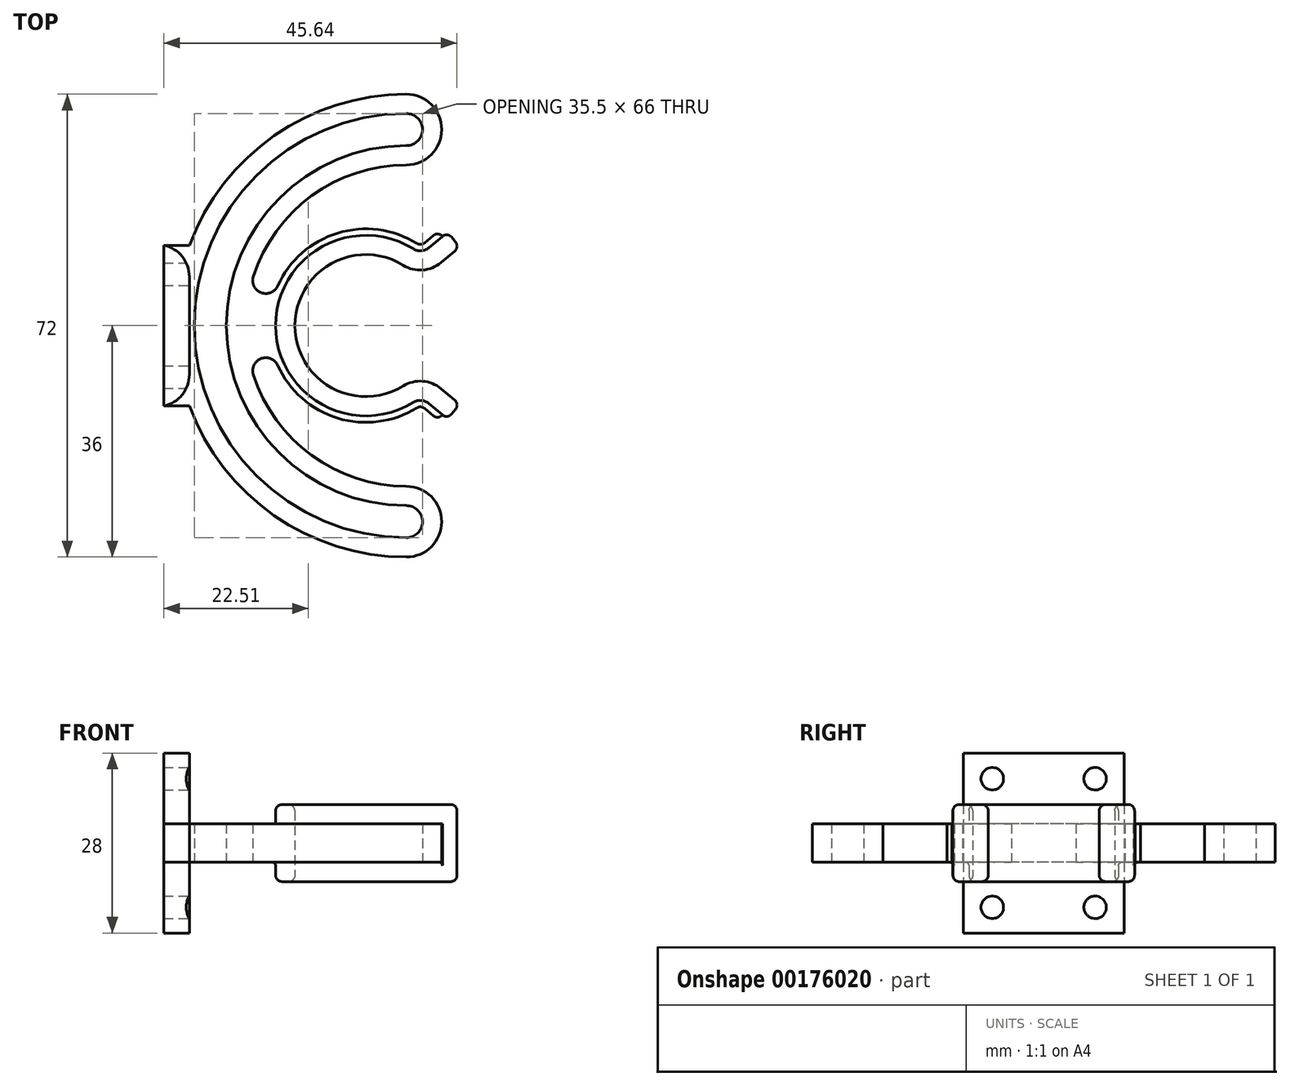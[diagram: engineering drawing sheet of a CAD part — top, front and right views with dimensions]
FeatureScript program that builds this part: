
annotation { "Feature Type Name" : "Feature", "Feature Type Description" : "" }
export const myFeature = defineFeature(function(context is Context, id is Id, definition is map)
    precondition{}
    {
        {
            var Q0;
            Q0=qCreatedBy(makeId("Top.planeOp"),FACE);
            var sketch = newSketch(context, id + "F0", { "sketchPlane" : qUnion([Q0])});
            skArc(sketch, "E0", {"start": v(5.83, 9.39) * mm, "mid": v(-5.37, 9.66) * mm, "end": v(-11.05, 0) * mm});
            skLineSegment(sketch, "E1", {"start": v(0, 0) * mm, "end": v(8.46, 7.1) * mm, "construction": true});
            skArc(sketch, "E2.0", {"start": v(7.41, 11.93) * mm, "mid": v(-6.83, 12.28) * mm, "end": v(-14.05, 0) * mm});
            skLineSegment(sketch, "E3", {"start": v(11.68, 9.8) * mm, "end": v(13.83, 11.6) * mm});
            skLineSegment(sketch, "E4", {"start": v(13.95, 13.01) * mm, "end": v(13.3, 13.78) * mm});
            skLineSegment(sketch, "E5", {"start": v(11.9, 13.9) * mm, "end": v(9.75, 12.1) * mm});
            skPoint(sketch, "E6.visualSharp", {"position": v(8.59, 11.12) * mm});
            skArc(sketch, "E6.filletArc", {"start": v(7.41, 11.93) * mm, "mid": v(8.61, 11.64) * mm, "end": v(9.75, 12.1) * mm});
            skPoint(sketch, "E7.visualSharp", {"position": v(12.66, 14.54) * mm});
            skArc(sketch, "E7.filletArc", {"start": v(13.3, 13.78) * mm, "mid": v(12.63, 14.13) * mm, "end": v(11.9, 13.9) * mm});
            skPoint(sketch, "E8.visualSharp", {"position": v(14.6, 12.25) * mm});
            skArc(sketch, "E8.filletArc", {"start": v(13.83, 11.6) * mm, "mid": v(14.18, 12.28) * mm, "end": v(13.95, 13.01) * mm});
            skPoint(sketch, "E9.visualSharp", {"position": v(8.46, 7.1) * mm});
            skArc(sketch, "E9.filletArc", {"start": v(5.83, 9.39) * mm, "mid": v(8.82, 8.65) * mm, "end": v(11.68, 9.8) * mm});
            skLineSegment(sketch, "E10", {"start": v(-14.05, 0) * mm, "end": v(0, 0) * mm, "construction": true});
            skArc(sketch, "E11.MirrorCS", {"start": v(5.83, -9.39) * mm, "mid": v(-5.37, -9.66) * mm, "end": v(-11.05, 0) * mm});
            skArc(sketch, "E12.MirrorCS", {"start": v(5.83, -9.39) * mm, "mid": v(8.82, -8.65) * mm, "end": v(11.68, -9.8) * mm});
            skLineSegment(sketch, "E13.MirrorCS", {"start": v(11.68, -9.8) * mm, "end": v(13.83, -11.6) * mm});
            skArc(sketch, "E14.MirrorCS", {"start": v(13.83, -11.6) * mm, "mid": v(14.18, -12.28) * mm, "end": v(13.95, -13.01) * mm});
            skLineSegment(sketch, "E15.MirrorCS", {"start": v(13.95, -13.01) * mm, "end": v(13.3, -13.78) * mm});
            skArc(sketch, "E16.MirrorCS", {"start": v(13.3, -13.78) * mm, "mid": v(12.63, -14.13) * mm, "end": v(11.9, -13.9) * mm});
            skLineSegment(sketch, "E17.MirrorCS", {"start": v(11.9, -13.9) * mm, "end": v(9.75, -12.1) * mm});
            skArc(sketch, "E18.MirrorCS", {"start": v(7.41, -11.93) * mm, "mid": v(8.61, -11.64) * mm, "end": v(9.75, -12.1) * mm});
            skArc(sketch, "E19.MirrorCS", {"start": v(7.41, -11.93) * mm, "mid": v(-6.83, -12.28) * mm, "end": v(-14.05, 0) * mm});
            skSolve(sketch);
        }
        {
            var Q0;
            Q0=qCreatedBy(makeId("Top.planeOp"),FACE);
            var sketch = newSketch(context, id + "F1", { "sketchPlane" : qUnion([Q0])});
            skLineSegment(sketch, "E20.0", {"start": v(10.49, -14.02) * mm, "end": v(9.11, -12.87) * mm});
            skArc(sketch, "E20.1", {"start": v(7.94, -12.78) * mm, "mid": v(-4.39, -14.4) * mm, "end": v(-13.72, -6.18) * mm});
            skArc(sketch, "E20.2", {"start": v(7.94, 12.78) * mm, "mid": v(-4.39, 14.4) * mm, "end": v(-13.72, 6.18) * mm});
            skLineSegment(sketch, "E20.3", {"start": v(10.49, 14.02) * mm, "end": v(9.11, 12.87) * mm});
            skLineSegment(sketch, "E21.0", {"start": v(11.9, -13.9) * mm, "end": v(8.59, -11.12) * mm});
            skArc(sketch, "E21.1", {"start": v(8.59, -11.12) * mm, "mid": v(-6.2, -12.61) * mm, "end": v(-14.05, 0) * mm});
            skArc(sketch, "E21.2", {"start": v(8.59, 11.12) * mm, "mid": v(-6.2, 12.61) * mm, "end": v(-14.05, 0) * mm});
            skLineSegment(sketch, "E21.3", {"start": v(11.9, 13.9) * mm, "end": v(8.59, 11.12) * mm});
            skLineSegment(sketch, "E22", {"start": v(11.9, 13.9) * mm, "end": v(11.9, 13.9) * mm});
            skLineSegment(sketch, "E23", {"start": v(11.9, -13.9) * mm, "end": v(11.9, -13.9) * mm});
            skPoint(sketch, "E24.visualSharp", {"position": v(11.26, -14.67) * mm});
            skArc(sketch, "E24.filletArc", {"start": v(10.49, -14.02) * mm, "mid": v(11.22, -14.25) * mm, "end": v(11.9, -13.9) * mm});
            skPoint(sketch, "E25.visualSharp", {"position": v(11.26, 14.67) * mm});
            skArc(sketch, "E25.filletArc", {"start": v(11.9, 13.9) * mm, "mid": v(11.22, 14.25) * mm, "end": v(10.49, 14.02) * mm});
            skPoint(sketch, "E26.visualSharp", {"position": v(8.54, 12.4) * mm});
            skArc(sketch, "E26.filletArc", {"start": v(7.94, 12.78) * mm, "mid": v(8.54, 12.64) * mm, "end": v(9.11, 12.87) * mm});
            skPoint(sketch, "E27.visualSharp", {"position": v(8.54, -12.4) * mm});
            skArc(sketch, "E27.filletArc", {"start": v(9.11, -12.87) * mm, "mid": v(8.54, -12.64) * mm, "end": v(7.94, -12.78) * mm});
            skLineSegment(sketch, "E28.bottom", {"start": v(-15.55, 5) * mm, "end": v(-15.6, 5) * mm});
            skLineSegment(sketch, "E28.top", {"start": v(-15.55, -5) * mm, "end": v(-15.6, -5) * mm});
            skPoint(sketch, "E28.middle", {"position": v(-16.2, 0) * mm});
            skArc(sketch, "E29", {"start": v(-17.51, -7.6) * mm, "mid": v(-8.44, -20.19) * mm, "end": v(6.3, -25) * mm});
            skLineSegment(sketch, "E30", {"start": v(6.3, -25) * mm, "end": v(6.3, 25) * mm, "construction": true});
            skArc(sketch, "E31.trimOffspring", {"start": v(6.3, 25) * mm, "mid": v(-8.44, 20.19) * mm, "end": v(-17.51, 7.6) * mm});
            skArc(sketch, "E32", {"start": v(6.3, 28) * mm, "mid": v(-21.7, 0) * mm, "end": v(6.3, -28) * mm});
            skLineSegment(sketch, "E33", {"start": v(6.3, 25) * mm, "end": v(6.3, 28) * mm, "construction": true});
            skLineSegment(sketch, "E34", {"start": v(6.3, -25) * mm, "end": v(6.3, -28) * mm, "construction": true});
            skLineSegment(sketch, "E35", {"start": v(6.3, 28) * mm, "end": v(6.3, 33) * mm, "construction": true});
            skLineSegment(sketch, "E36", {"start": v(6.3, 33) * mm, "end": v(6.3, 36) * mm, "construction": true});
            skArc(sketch, "E37", {"start": v(6.3, 33) * mm, "mid": v(-26.7, 0) * mm, "end": v(6.3, -33) * mm});
            skArc(sketch, "E38", {"start": v(6.3, 36) * mm, "mid": v(-29.7, 0) * mm, "end": v(6.3, -36) * mm});
            skLineSegment(sketch, "E39", {"start": v(6.3, -28) * mm, "end": v(6.3, -33) * mm, "construction": true});
            skLineSegment(sketch, "E40", {"start": v(6.3, -33) * mm, "end": v(6.3, -36) * mm, "construction": true});
            skArc(sketch, "E41", {"start": v(6.3, 28) * mm, "mid": v(8.8, 30.5) * mm, "end": v(6.3, 33) * mm});
            skArc(sketch, "E42", {"start": v(6.3, 25) * mm, "mid": v(11.8, 30.5) * mm, "end": v(6.3, 36) * mm});
            skArc(sketch, "E43", {"start": v(6.3, -33) * mm, "mid": v(8.8, -30.5) * mm, "end": v(6.3, -28) * mm});
            skArc(sketch, "E44", {"start": v(6.3, -36) * mm, "mid": v(11.8, -30.5) * mm, "end": v(6.3, -25) * mm});
            skLineSegment(sketch, "E45", {"start": v(9.11, 12.87) * mm, "end": v(9.75, 12.1) * mm, "construction": true});
            skPoint(sketch, "E46.visualSharp", {"position": v(-18.2, 5) * mm});
            skArc(sketch, "E46.filletArc", {"start": v(-17.51, 7.6) * mm, "mid": v(-17.22, 5.82) * mm, "end": v(-15.6, 5) * mm});
            skPoint(sketch, "E47.visualSharp", {"position": v(-18.2, -5) * mm});
            skArc(sketch, "E47.filletArc", {"start": v(-15.6, -5) * mm, "mid": v(-17.22, -5.82) * mm, "end": v(-17.51, -7.6) * mm});
            skPoint(sketch, "E48.visualSharp", {"position": v(-14.2, -5) * mm});
            skArc(sketch, "E48.filletArc", {"start": v(-13.72, -6.18) * mm, "mid": v(-14.46, -5.32) * mm, "end": v(-15.55, -5) * mm});
            skPoint(sketch, "E49.visualSharp", {"position": v(-14.2, 5) * mm});
            skArc(sketch, "E49.filletArc", {"start": v(-15.55, 5) * mm, "mid": v(-14.46, 5.32) * mm, "end": v(-13.72, 6.18) * mm});
            skSolve(sketch);
        }
        {
            var Q0;
            Q0 = qSketchRegion(id + "F0", true);
            extrude(context, id + "F2", {"entities" : qUnion([Q0]), "endBound" : BoundingType.SYMMETRIC, "depth" : 12 * mm});
        }
        {
            var Q0;
            Q0 = qSketchRegion(id + "F1", true);
            extrude(context, id + "F3", {"entities" : qUnion([Q0]), "operationType" : NewBodyOperationType.ADD, "endBound" : BoundingType.SYMMETRIC, "depth" : 6 * mm});
        }
        {
            var Q0;
            Q0=makeQuery(id+"F2.opExtrude","CAP_EDGE",EDGE,{"disambiguationData":[OSD([sQuery(id+"F0.wireOp",EDGE,"E9.filletArc")])],"isStart":true});
            var Q1;
            Q1=makeQuery(id+"F2.opExtrude","CAP_EDGE",EDGE,{"disambiguationData":[OSD([sQuery(id+"F0.wireOp",EDGE,"E9.filletArc")])],"isStart":false});
            fillet(context, id + "F4", {"entities" : qUnion([Q0, Q1]), "radius" : 1 * mm, "tangentPropagation" : true, "allowEdgeOverflow" : false});
        }
        {
            var Q0;
            Q0=makeQuery(id+"F3.opExtrude","CAP_EDGE",EDGE,{"disambiguationData":[OSD([sQuery(id+"F1.wireOp",EDGE,"E21.1"),sQuery(id+"F1.wireOp",EDGE,"E21.2")])],"isStart":true});
            var Q1;
            Q1=makeQuery(id+"F3.opExtrude","CAP_EDGE",EDGE,{"disambiguationData":[OSD([sQuery(id+"F1.wireOp",EDGE,"E21.1"),sQuery(id+"F1.wireOp",EDGE,"E21.2")])],"isStart":false});
            fillet(context, id + "F5", {"entities" : qUnion([Q0, Q1]), "radius" : .5 * mm, "tangentPropagation" : true, "allowEdgeOverflow" : false});
        }
        {
            var Q0;
            Q0=qCreatedBy(makeId("Top.planeOp"),FACE);
            var sketch = newSketch(context, id + "F6", { "sketchPlane" : qUnion([Q0])});
            skLineSegment(sketch, "E50.bottom", {"start": v(-31.46, -12.5) * mm, "end": v(-27.46, -12.5) * mm});
            skLineSegment(sketch, "E50.top", {"start": v(-31.46, 12.5) * mm, "end": v(-27.46, 12.5) * mm});
            skLineSegment(sketch, "E50.left", {"start": v(-31.46, -12.5) * mm, "end": v(-31.46, 12.5) * mm});
            skLineSegment(sketch, "E50.right", {"start": v(-27.46, -12.5) * mm, "end": v(-27.46, 12.5) * mm});
            skPoint(sketch, "E50.middle", {"position": v(-29.46, 0) * mm});
            skSolve(sketch);
        }
        {
            var Q0;
            Q0 = qSketchRegion(id + "F6", true);
            extrude(context, id + "F7", {"entities" : qUnion([Q0]), "operationType" : NewBodyOperationType.ADD, "endBound" : BoundingType.SYMMETRIC, "depth" : 28 * mm});
        }
        {
            var Q0;
            {var subQ0=sQuery(id+"F6.wireOp",EDGE,"E50.bottom");var subQ1=sQuery(id+"F1.wireOp",EDGE,"E38");var subQ2=sQuery(id+"F1.wireOp",EDGE,"E49.filletArc");var subQ3=sQuery(id+"F1.wireOp",EDGE,"E48.filletArc");var subQ4=sQuery(id+"F1.wireOp",EDGE,"E47.filletArc");var subQ5=sQuery(id+"F1.wireOp",EDGE,"E46.filletArc");var subQ6=sQuery(id+"F1.wireOp",EDGE,"E44");var subQ7=sQuery(id+"F1.wireOp",EDGE,"E43");var subQ8=sQuery(id+"F1.wireOp",EDGE,"E42");var subQ9=sQuery(id+"F1.wireOp",EDGE,"E41");var subQ10=sQuery(id+"F1.wireOp",EDGE,"E37");var subQ11=sQuery(id+"F1.wireOp",EDGE,"E32");var subQ12=sQuery(id+"F1.wireOp",EDGE,"E31.trimOffspring");var subQ13=sQuery(id+"F1.wireOp",EDGE,"E29");var subQ14=sQuery(id+"F1.wireOp",EDGE,"E28.top");var subQ15=sQuery(id+"F1.wireOp",EDGE,"E28.bottom");var subQ16=sQuery(id+"F1.wireOp",EDGE,"E27.filletArc");var subQ17=sQuery(id+"F1.wireOp",EDGE,"E26.filletArc");var subQ18=sQuery(id+"F1.wireOp",EDGE,"E25.filletArc");var subQ19=sQuery(id+"F1.wireOp",EDGE,"E24.filletArc");var subQ20=sQuery(id+"F1.wireOp",EDGE,"E21.3");var subQ21=sQuery(id+"F1.wireOp",EDGE,"E21.2");var subQ22=sQuery(id+"F1.wireOp",EDGE,"E21.1");var subQ23=sQuery(id+"F1.wireOp",EDGE,"E21.0");var subQ24=sQuery(id+"F1.wireOp",EDGE,"E20.3");var subQ25=sQuery(id+"F1.wireOp",EDGE,"E20.2");var subQ26=sQuery(id+"F1.wireOp",EDGE,"E20.1");var subQ27=sQuery(id+"F1.wireOp",EDGE,"E20.0");var subQ28=sQuery(id+"F6.wireOp",EDGE,"E50.right");Q0=makeQuery(id+"F7.boolean.opBoolean","SPLIT",EDGE,{"disambiguationData":[TD([makeQuery(id+"F3.opExtrude","CAP_FACE",FACE,{"disambiguationData":[OSD([subQ27,subQ26,subQ25,subQ24,subQ23,subQ22,subQ21,subQ20,subQ19,subQ18,subQ17,subQ16,subQ15,subQ14,subQ13,subQ12,subQ11,subQ10,subQ1,subQ9,subQ8,subQ7,subQ6,subQ5,subQ4,subQ3,subQ2])],"isStart":true}),makeQuery(id+"F3.opExtrude","CAP_FACE",FACE,{"disambiguationData":[OSD([subQ27,subQ26,subQ25,subQ24,subQ23,subQ22,subQ21,subQ20,subQ19,subQ18,subQ17,subQ16,subQ15,subQ14,subQ13,subQ12,subQ11,subQ10,subQ1,subQ9,subQ8,subQ7,subQ6,subQ5,subQ4,subQ3,subQ2])],"isStart":false}),makeQuery(id+"F3.opExtrude","SWEPT_FACE",FACE,{"disambiguationData":[OSD([subQ1])]}),makeQuery(id+"F7.opExtrude","SWEPT_FACE",FACE,{"disambiguationData":[OSD([subQ0])]}),makeQuery(id+"F7.opExtrude","SWEPT_FACE",FACE,{"disambiguationData":[OSD([subQ28])]})])],"derivedFrom":makeQuery(id+"F7.opExtrude","SWEPT_EDGE",EDGE,{"disambiguationData":[OSD([subQ0,subQ28])]})});}
            var Q1;
            {var subQ0=sQuery(id+"F6.wireOp",EDGE,"E50.top");var subQ1=sQuery(id+"F1.wireOp",EDGE,"E38");var subQ2=sQuery(id+"F1.wireOp",EDGE,"E49.filletArc");var subQ3=sQuery(id+"F1.wireOp",EDGE,"E48.filletArc");var subQ4=sQuery(id+"F1.wireOp",EDGE,"E47.filletArc");var subQ5=sQuery(id+"F1.wireOp",EDGE,"E46.filletArc");var subQ6=sQuery(id+"F1.wireOp",EDGE,"E44");var subQ7=sQuery(id+"F1.wireOp",EDGE,"E43");var subQ8=sQuery(id+"F1.wireOp",EDGE,"E42");var subQ9=sQuery(id+"F1.wireOp",EDGE,"E41");var subQ10=sQuery(id+"F1.wireOp",EDGE,"E37");var subQ11=sQuery(id+"F1.wireOp",EDGE,"E32");var subQ12=sQuery(id+"F1.wireOp",EDGE,"E31.trimOffspring");var subQ13=sQuery(id+"F1.wireOp",EDGE,"E29");var subQ14=sQuery(id+"F1.wireOp",EDGE,"E28.top");var subQ15=sQuery(id+"F1.wireOp",EDGE,"E28.bottom");var subQ16=sQuery(id+"F1.wireOp",EDGE,"E27.filletArc");var subQ17=sQuery(id+"F1.wireOp",EDGE,"E26.filletArc");var subQ18=sQuery(id+"F1.wireOp",EDGE,"E25.filletArc");var subQ19=sQuery(id+"F1.wireOp",EDGE,"E24.filletArc");var subQ20=sQuery(id+"F1.wireOp",EDGE,"E21.3");var subQ21=sQuery(id+"F1.wireOp",EDGE,"E21.2");var subQ22=sQuery(id+"F1.wireOp",EDGE,"E21.1");var subQ23=sQuery(id+"F1.wireOp",EDGE,"E21.0");var subQ24=sQuery(id+"F1.wireOp",EDGE,"E20.3");var subQ25=sQuery(id+"F1.wireOp",EDGE,"E20.2");var subQ26=sQuery(id+"F1.wireOp",EDGE,"E20.1");var subQ27=sQuery(id+"F1.wireOp",EDGE,"E20.0");var subQ28=sQuery(id+"F6.wireOp",EDGE,"E50.right");Q1=makeQuery(id+"F7.boolean.opBoolean","SPLIT",EDGE,{"disambiguationData":[TD([makeQuery(id+"F3.opExtrude","CAP_FACE",FACE,{"disambiguationData":[OSD([subQ27,subQ26,subQ25,subQ24,subQ23,subQ22,subQ21,subQ20,subQ19,subQ18,subQ17,subQ16,subQ15,subQ14,subQ13,subQ12,subQ11,subQ10,subQ1,subQ9,subQ8,subQ7,subQ6,subQ5,subQ4,subQ3,subQ2])],"isStart":true}),makeQuery(id+"F3.opExtrude","CAP_FACE",FACE,{"disambiguationData":[OSD([subQ27,subQ26,subQ25,subQ24,subQ23,subQ22,subQ21,subQ20,subQ19,subQ18,subQ17,subQ16,subQ15,subQ14,subQ13,subQ12,subQ11,subQ10,subQ1,subQ9,subQ8,subQ7,subQ6,subQ5,subQ4,subQ3,subQ2])],"isStart":false}),makeQuery(id+"F3.opExtrude","SWEPT_FACE",FACE,{"disambiguationData":[OSD([subQ1])]}),makeQuery(id+"F7.opExtrude","SWEPT_FACE",FACE,{"disambiguationData":[OSD([subQ0])]}),makeQuery(id+"F7.opExtrude","SWEPT_FACE",FACE,{"disambiguationData":[OSD([subQ28])]})])],"derivedFrom":makeQuery(id+"F7.opExtrude","SWEPT_EDGE",EDGE,{"disambiguationData":[OSD([subQ0,subQ28])]})});}
            fillet(context, id + "F8", {"entities" : qUnion([Q0, Q1]), "radius" : 5 * mm, "tangentPropagation" : true, "allowEdgeOverflow" : false});
        }
        {
            var Q0;
            {var subQ0=sQuery(id+"F6.wireOp",EDGE,"E50.right");var subQ1=sQuery(id+"F6.wireOp",EDGE,"E50.top");var subQ2=sQuery(id+"F6.wireOp",EDGE,"E50.bottom");Q0=makeQuery(id+"F7.boolean.opBoolean","SPLIT",FACE,{"disambiguationData":[TD([makeQuery(id+"F7.opExtrude","CAP_FACE",FACE,{"disambiguationData":[OSD([subQ2,subQ1,sQuery(id+"F6.wireOp",EDGE,"E50.left"),subQ0])],"isStart":true})])],"derivedFrom":makeQuery(id+"F7.opExtrude","SWEPT_FACE",FACE,{"disambiguationData":[OSD([subQ0])]})});}
            var sketch = newSketch(context, id + "F9", { "sketchPlane" : qUnion([Q0])});
            skLineSegment(sketch, "E51.bottom", {"start": v(-8, -10) * mm, "end": v(8, -10) * mm, "construction": true});
            skLineSegment(sketch, "E51.top", {"start": v(-8, 10) * mm, "end": v(8, 10) * mm, "construction": true});
            skLineSegment(sketch, "E51.left", {"start": v(-8, -10) * mm, "end": v(-8, 10) * mm, "construction": true});
            skLineSegment(sketch, "E51.right", {"start": v(8, -10) * mm, "end": v(8, 10) * mm, "construction": true});
            skPoint(sketch, "E51.middle", {"position": v(0, 0) * mm});
            skCircle(sketch, "E52", {"center": v(-8, -10) * mm, "radius": 1.75 * mm});
            skCircle(sketch, "E53", {"center": v(-8, 10) * mm, "radius": 1.75 * mm});
            skCircle(sketch, "E54", {"center": v(8, 10) * mm, "radius": 1.75 * mm});
            skCircle(sketch, "E55", {"center": v(8, -10) * mm, "radius": 1.75 * mm});
            skSolve(sketch);
        }
        {
            var Q0;
            Q0 = qSketchRegion(id + "F9", true);
            extrude(context, id + "F10", {"entities" : qUnion([Q0]), "operationType" : NewBodyOperationType.REMOVE, "endBound" : BoundingType.THROUGH_ALL, "oppositeDirection" : true, "depth" : 25 * mm});
        }
    });
